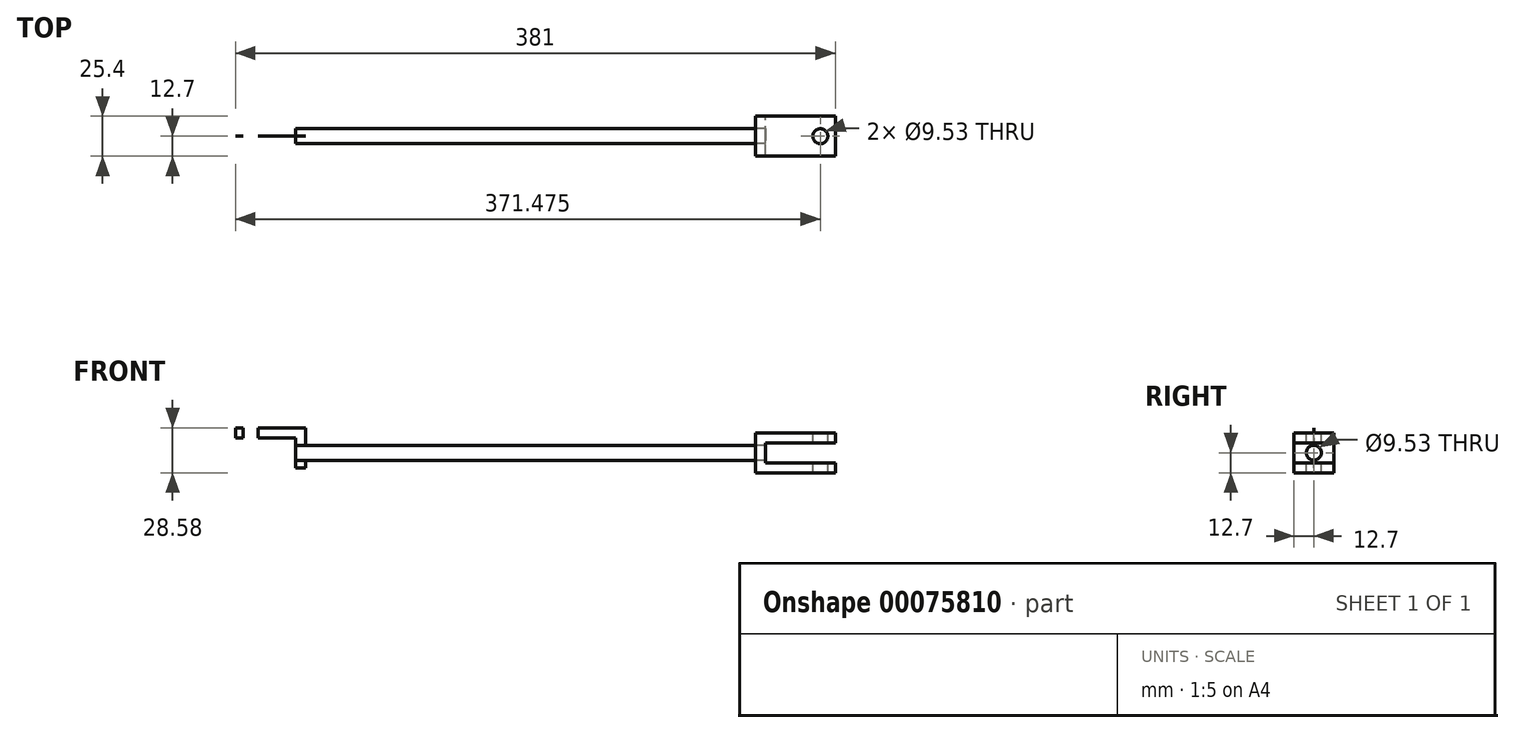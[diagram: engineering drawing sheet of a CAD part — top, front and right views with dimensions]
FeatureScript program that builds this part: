
annotation { "Feature Type Name" : "Feature", "Feature Type Description" : "" }
export const myFeature = defineFeature(function(context is Context, id is Id, definition is map)
    precondition{}
    {
        {
            var Q0;
            Q0=qCreatedBy(makeId("Right.planeOp"),FACE);
            var sketch = newSketch(context, id + "F0", { "sketchPlane" : qUnion([Q0])});
            skCircle(sketch, "E0", {"center": v(0, 0) * mm, "radius": 4.76 * mm});
            skSolve(sketch);
        }
        {
            var Q0;
            Q0 = qSketchRegion(id + "F0", true);
            extrude(context, id + "F1", {"entities" : qUnion([Q0]), "depth" : 298.45 * mm});
        }
        {
            var Q0;
            Q0=qCreatedBy(makeId("Front.planeOp"),FACE);
            var sketch = newSketch(context, id + "F2", { "sketchPlane" : qUnion([Q0])});
            skLineSegment(sketch, "E1", {"start": v(0, 9.52) * mm, "end": v(0, -9.52) * mm});
            skLineSegment(sketch, "E2", {"start": v(0, -9.52) * mm, "end": v(6.35, -9.52) * mm});
            skLineSegment(sketch, "E3", {"start": v(6.35, -9.52) * mm, "end": v(6.35, 15.88) * mm});
            skLineSegment(sketch, "E4", {"start": v(6.35, 15.88) * mm, "end": v(-38.1, 15.88) * mm});
            skLineSegment(sketch, "E5", {"start": v(-38.1, 15.88) * mm, "end": v(-38.1, 9.52) * mm});
            skLineSegment(sketch, "E6", {"start": v(-38.1, 9.52) * mm, "end": v(0, 9.52) * mm});
            skSolve(sketch);
        }
        {
            var Q0;
            Q0 = qSketchRegion(id + "F2", true);
            extrude(context, id + "F3", {"entities" : qUnion([Q0]), "endBound" : BoundingType.SYMMETRIC, "depth" : 3 / 101.6 * mm});
        }
        {
            var Q0;
            Q0=makeQuery(id+"F1.opExtrude","SWEPT_BODY",BODY,{"disambiguationData":[OSD([sQuery(id+"F0.wireOp",EDGE,"E0")])]});
            var Q1;
            Q1=makeQuery(id+"F3.opExtrude","SWEPT_BODY",BODY,{"disambiguationData":[OSD([sQuery(id+"F2.wireOp",EDGE,"E1"),sQuery(id+"F2.wireOp",EDGE,"E2"),sQuery(id+"F2.wireOp",EDGE,"E3"),sQuery(id+"F2.wireOp",EDGE,"E4"),sQuery(id+"F2.wireOp",EDGE,"E5"),sQuery(id+"F2.wireOp",EDGE,"E6")])]});
            booleanBodies(context, id + "F4", {"operationType" : BooleanOperationType.SUBTRACTION, "tools" : qUnion([Q0]), "targets" : qUnion([Q1]), "keepTools" : true});
        }
        {
            var Q0;
            Q0=makeQuery(id+"F3.opExtrude","SWEPT_FACE",FACE,{"disambiguationData":[OSD([sQuery(id+"F2.wireOp",EDGE,"E4")])]});
            var sketch = newSketch(context, id + "F5", { "sketchPlane" : qUnion([Q0])});
            skCircle(sketch, "E7", {"center": v(-28.58, 0) * mm, "radius": 4.76 * mm});
            skPoint(sketch, "E7.centerSnap0", {"position": v(-38.1, 0) * mm});
            skSolve(sketch);
        }
        {
            var Q0;
            Q0 = qSketchRegion(id + "F5", true);
            extrude(context, id + "F6", {"entities" : qUnion([Q0]), "operationType" : NewBodyOperationType.REMOVE, "endBound" : BoundingType.THROUGH_ALL, "oppositeDirection" : true, "depth" : 25 * mm});
        }
        {
            var Q0;
            Q0=qCreatedBy(makeId("Front.planeOp"),FACE);
            var sketch = newSketch(context, id + "F7", { "sketchPlane" : qUnion([Q0])});
            skLineSegment(sketch, "E8", {"start": v(292.1, 12.7) * mm, "end": v(292.1, -12.7) * mm});
            skLineSegment(sketch, "E9", {"start": v(292.1, -12.7) * mm, "end": v(342.9, -12.7) * mm});
            skLineSegment(sketch, "E10", {"start": v(342.9, -12.7) * mm, "end": v(342.9, -6.35) * mm});
            skLineSegment(sketch, "E11", {"start": v(342.9, -6.35) * mm, "end": v(298.45, -6.35) * mm});
            skLineSegment(sketch, "E12", {"start": v(298.45, -6.35) * mm, "end": v(298.45, 6.35) * mm});
            skLineSegment(sketch, "E13", {"start": v(298.45, 6.35) * mm, "end": v(342.9, 6.35) * mm});
            skLineSegment(sketch, "E14", {"start": v(342.9, 6.35) * mm, "end": v(342.9, 12.7) * mm});
            skLineSegment(sketch, "E15", {"start": v(342.9, 12.7) * mm, "end": v(292.1, 12.7) * mm});
            skPoint(sketch, "E16", {"position": v(292.1, 0) * mm});
            skSolve(sketch);
        }
        {
            var Q0;
            Q0 = qSketchRegion(id + "F7", true);
            extrude(context, id + "F8", {"entities" : qUnion([Q0]), "endBound" : BoundingType.SYMMETRIC, "depth" : 25.4 * mm});
        }
        {
            var Q0;
            Q0=makeQuery(id+"F1.opExtrude","SWEPT_BODY",BODY,{"disambiguationData":[OSD([sQuery(id+"F0.wireOp",EDGE,"E0")])]});
            var Q1;
            Q1=makeQuery(id+"F8.opExtrude","SWEPT_BODY",BODY,{"disambiguationData":[OSD([sQuery(id+"F7.wireOp",EDGE,"E8"),sQuery(id+"F7.wireOp",EDGE,"E9"),sQuery(id+"F7.wireOp",EDGE,"E10"),sQuery(id+"F7.wireOp",EDGE,"E11"),sQuery(id+"F7.wireOp",EDGE,"E12"),sQuery(id+"F7.wireOp",EDGE,"E13"),sQuery(id+"F7.wireOp",EDGE,"E14"),sQuery(id+"F7.wireOp",EDGE,"E15")])]});
            booleanBodies(context, id + "F9", {"operationType" : BooleanOperationType.SUBTRACTION, "tools" : qUnion([Q0]), "targets" : qUnion([Q1]), "keepTools" : true});
        }
        {
            var Q0;
            Q0=makeQuery(id+"F8.opExtrude","SWEPT_FACE",FACE,{"disambiguationData":[OSD([sQuery(id+"F7.wireOp",EDGE,"E15")])]});
            var sketch = newSketch(context, id + "F10", { "sketchPlane" : qUnion([Q0])});
            skCircle(sketch, "E17", {"center": v(333.38, 0) * mm, "radius": 4.76 * mm});
            skPoint(sketch, "E17.centerSnap0", {"position": v(342.9, 0) * mm});
            skSolve(sketch);
        }
        {
            var Q0;
            Q0 = qSketchRegion(id + "F10", true);
            extrude(context, id + "F11", {"entities" : qUnion([Q0]), "operationType" : NewBodyOperationType.REMOVE, "endBound" : BoundingType.THROUGH_ALL, "oppositeDirection" : true, "depth" : 25 * mm});
        }
    });
